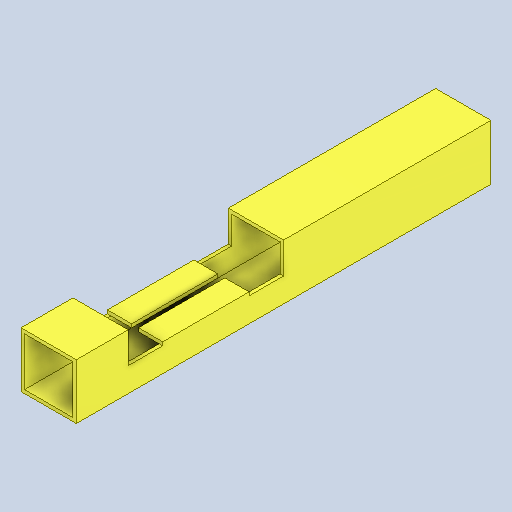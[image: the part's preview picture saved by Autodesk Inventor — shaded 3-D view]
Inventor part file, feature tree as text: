
AUTODESK INVENTOR PART (.ipt)
format: ipt  version: 2024.2 (Build 282272000, 272)  size: 107,520 bytes
history: native  units: in
note: dims shown in document units (in); Inventor stores cm internally (conversion verified against a paired STEP export)
features: mirror x1
ambient origin geometry x8: Origin, YZ Plane, XZ Plane, XY Plane, X Axis, Y Axis, Z Axis, Center Point
bodies: Solid1 (feature_tree)
feature tree (1):
  mirror  "Mirror1"
